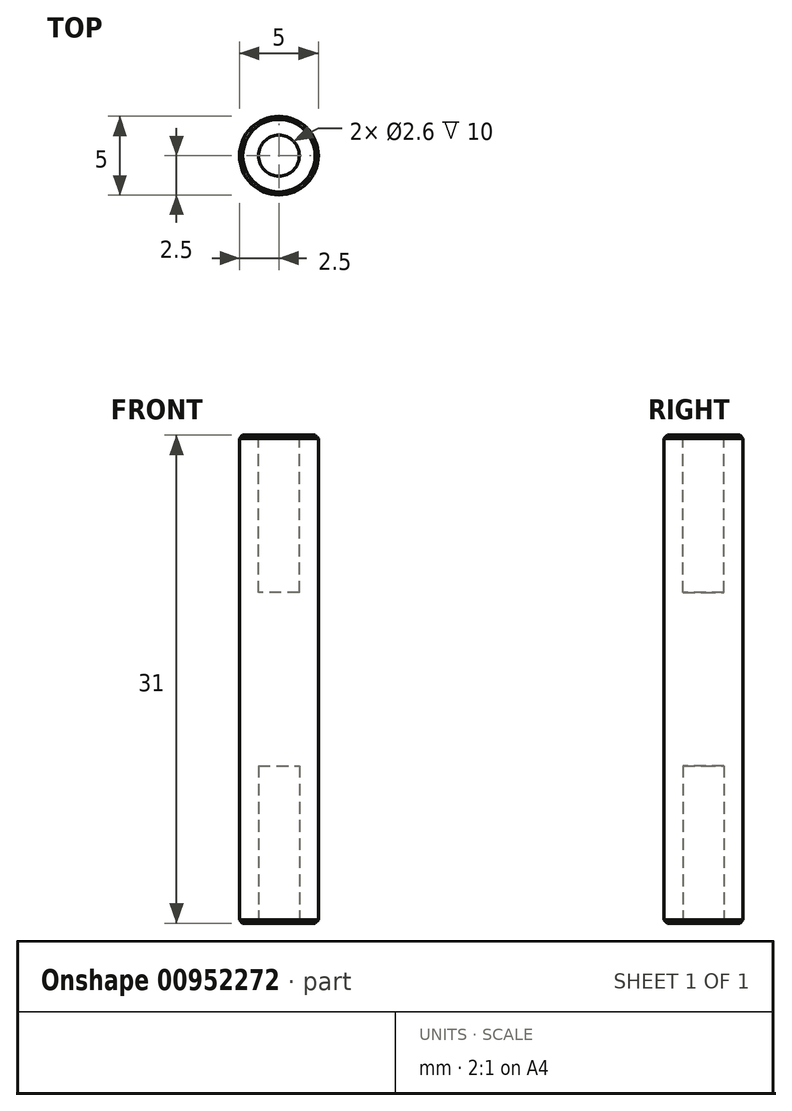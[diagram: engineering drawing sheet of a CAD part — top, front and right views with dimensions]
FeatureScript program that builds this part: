
annotation { "Feature Type Name" : "Feature", "Feature Type Description" : "" }
export const myFeature = defineFeature(function(context is Context, id is Id, definition is map)
    precondition{}
    {
        {
            var Q0;
            Q0=qCreatedBy(makeId("Top.planeOp"),FACE);
            var sketch = newSketch(context, id + "F0", { "sketchPlane" : qUnion([Q0])});
            skCircle(sketch, "E0", {"center": v(0, 0) * mm, "radius": 2.5 * mm});
            skSolve(sketch);
        }
        {
            var Q0;
            Q0 = qSketchRegion(id + "F0", true);
            extrude(context, id + "F1", {"entities" : qUnion([Q0]), "depth" : 31 * mm, "offsetDistance" : 25 * mm, "symmetric" : true});
        }
        {
            var Q0;
            Q0=makeQuery(id+"F1.opExtrude","CAP_FACE",FACE,{"disambiguationData":[OSD([sQuery(id+"F0.wireOp",EDGE,"E0")])],"isStart":false});
            var sketch = newSketch(context, id + "F2", { "sketchPlane" : qUnion([Q0])});
            skCircle(sketch, "E1", {"center": v(0, 0) * mm, "radius": 1.3 * mm});
            skSolve(sketch);
        }
        {
            var Q0;
            Q0 = qSketchRegion(id + "F2", true);
            extrude(context, id + "F3", {"entities" : qUnion([Q0]), "operationType" : NewBodyOperationType.REMOVE, "oppositeDirection" : true, "depth" : 10 * mm, "offsetDistance" : 25 * mm});
        }
        {
            var Q0;
            Q0=makeQuery(id+"F1.opExtrude","CAP_FACE",FACE,{"disambiguationData":[OSD([sQuery(id+"F0.wireOp",EDGE,"E0")])],"isStart":true});
            var sketch = newSketch(context, id + "F4", { "sketchPlane" : qUnion([Q0])});
            skCircle(sketch, "E2", {"center": v(0, 0) * mm, "radius": 1.3 * mm});
            skSolve(sketch);
        }
        {
            var Q0;
            Q0 = qSketchRegion(id + "F4", true);
            extrude(context, id + "F5", {"entities" : qUnion([Q0]), "operationType" : NewBodyOperationType.REMOVE, "oppositeDirection" : true, "depth" : 10 * mm, "offsetDistance" : 25 * mm});
        }
        {
            var Q0;
            Q0=makeQuery(id+"F1.opExtrude","SWEPT_FACE",FACE,{"disambiguationData":[OSD([sQuery(id+"F0.wireOp",EDGE,"E0")])]});
            chamfer(context, id + "F6", {"entities" : qUnion([Q0]), "width" : 0.2 * mm, "tangentPropagation" : true});
        }
    });
